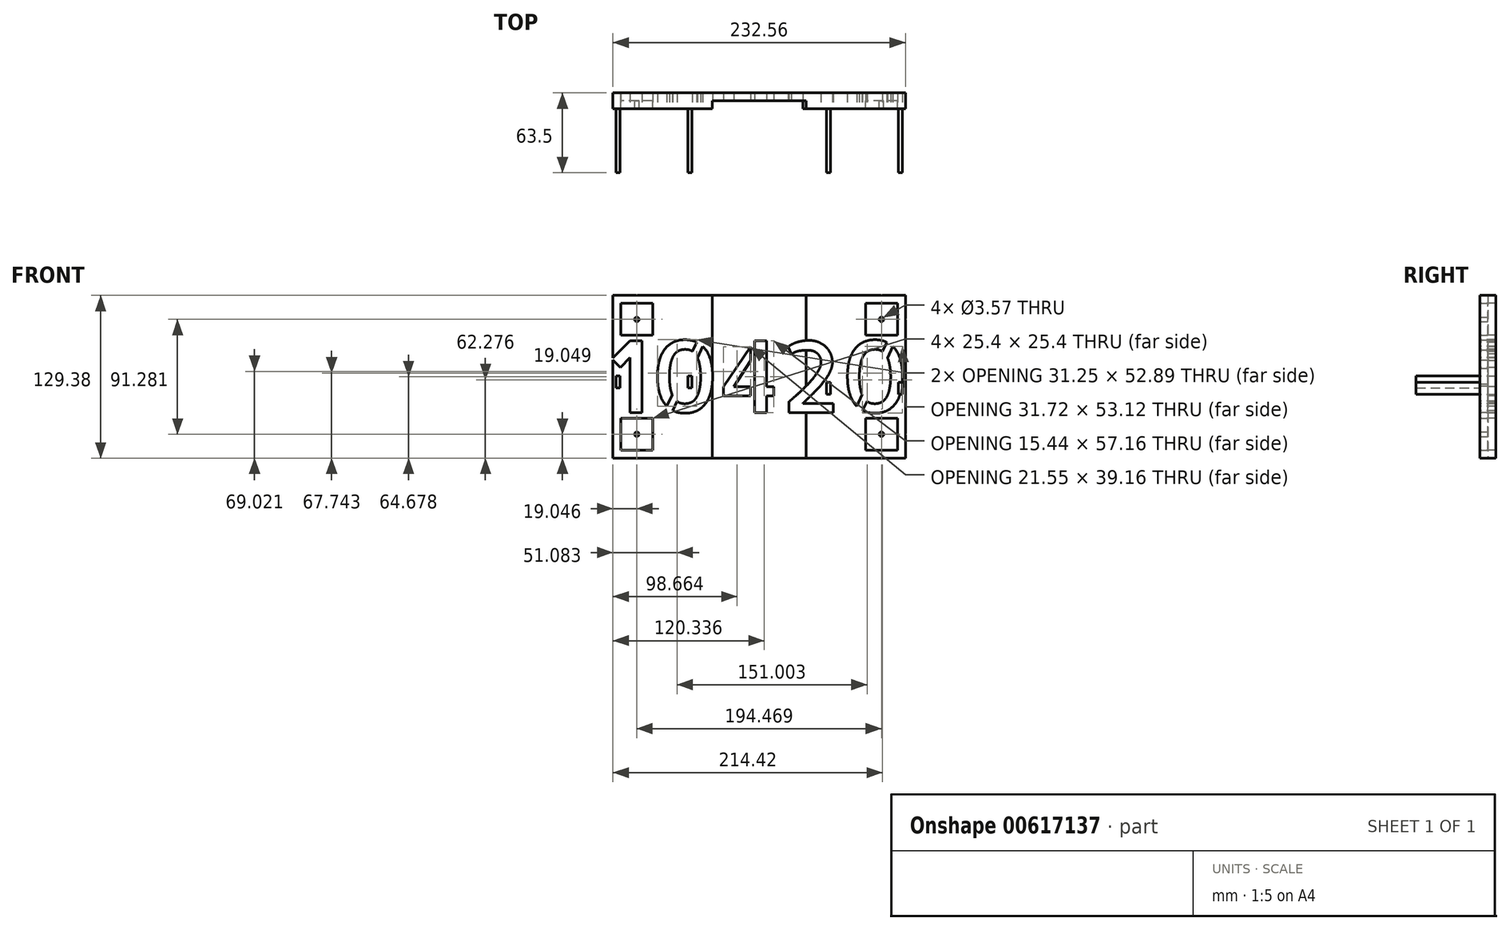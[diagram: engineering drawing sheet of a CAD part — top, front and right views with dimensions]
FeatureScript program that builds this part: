
annotation { "Feature Type Name" : "Feature", "Feature Type Description" : "" }
export const myFeature = defineFeature(function(context is Context, id is Id, definition is map)
    precondition{}
    {
        {
            var Q0;
            Q0=qCreatedBy(makeId("Front.planeOp"),FACE);
            var sketch = newSketch(context, id + "F0", { "sketchPlane" : qUnion([Q0])});
            skLineSegment(sketch, "E0.bottom", {"start": v(-116.28, 64.7) * mm, "end": v(116.28, 64.7) * mm});
            skLineSegment(sketch, "E0.top", {"start": v(-116.28, -64.7) * mm, "end": v(116.28, -64.7) * mm});
            skLineSegment(sketch, "E0.left", {"start": v(-116.28, 64.7) * mm, "end": v(-116.28, -64.7) * mm});
            skPoint(sketch, "E0.middle", {"position": v(0, 0) * mm});
            skLineSegment(sketch, "E1.bottom", {"start": v(-84.53, 32.94) * mm, "end": v(-109.93, 32.94) * mm});
            skLineSegment(sketch, "E1.top", {"start": v(-84.53, 58.34) * mm, "end": v(-109.93, 58.34) * mm});
            skLineSegment(sketch, "E1.left", {"start": v(-84.53, 32.94) * mm, "end": v(-84.53, 58.34) * mm});
            skLineSegment(sketch, "E1.right", {"start": v(-109.93, 32.94) * mm, "end": v(-109.93, 58.34) * mm});
            skLineSegment(sketch, "E2.bottom", {"start": v(-84.53, -58.34) * mm, "end": v(-109.93, -58.34) * mm});
            skLineSegment(sketch, "E2.top", {"start": v(-84.53, -32.94) * mm, "end": v(-109.93, -32.94) * mm});
            skLineSegment(sketch, "E2.left", {"start": v(-84.53, -58.34) * mm, "end": v(-84.53, -32.94) * mm});
            skLineSegment(sketch, "E2.right", {"start": v(-109.93, -58.34) * mm, "end": v(-109.93, -32.94) * mm});
            skPoint(sketch, "E2.middle", {"position": v(-97.23, -45.64) * mm});
            skLineSegment(sketch, "E3.bottom", {"start": v(109.93, 32.94) * mm, "end": v(84.53, 32.94) * mm});
            skLineSegment(sketch, "E3.top", {"start": v(109.93, 58.34) * mm, "end": v(84.53, 58.34) * mm});
            skLineSegment(sketch, "E3.left", {"start": v(109.93, 32.94) * mm, "end": v(109.93, 58.34) * mm});
            skLineSegment(sketch, "E3.right", {"start": v(84.53, 32.94) * mm, "end": v(84.53, 58.34) * mm});
            skPoint(sketch, "E3.middle", {"position": v(97.23, 45.64) * mm});
            skLineSegment(sketch, "E4", {"start": v(116.28, 64.7) * mm, "end": v(116.28, -64.7) * mm});
            skLineSegment(sketch, "E5.bottom", {"start": v(109.93, -58.34) * mm, "end": v(84.53, -58.34) * mm});
            skLineSegment(sketch, "E5.top", {"start": v(109.93, -32.94) * mm, "end": v(84.53, -32.94) * mm});
            skLineSegment(sketch, "E5.left", {"start": v(109.93, -58.34) * mm, "end": v(109.93, -32.94) * mm});
            skLineSegment(sketch, "E5.right", {"start": v(84.53, -58.34) * mm, "end": v(84.53, -32.94) * mm});
            skPoint(sketch, "E5.middle", {"position": v(97.23, -45.64) * mm});
            skPoint(sketch, "E6", {"position": v(-97.23, 45.64) * mm});
            skCircle(sketch, "E7", {"center": v(-97.23, 45.64) * mm, "radius": 1.79 * mm});
            skCircle(sketch, "E8", {"center": v(97.23, 45.64) * mm, "radius": 1.79 * mm});
            skCircle(sketch, "E9", {"center": v(-97.23, -45.64) * mm, "radius": 1.79 * mm});
            skCircle(sketch, "E10", {"center": v(97.23, -45.64) * mm, "radius": 1.79 * mm});
            skSolve(sketch);
        }
        {
            var Q0;
            Q0=makeQuery(id+"F0.imprint","IMPRINT",FACE,{"disambiguationData":[TD([[makeQuery(id+"F0.imprint","IMPRINT",EDGE,{"derivedFrom":sQuery(id+"F0.wireOp",EDGE,"E0.bottom")}),-1.0]])]});
            var Q1;
            Q1=makeQuery(id+"FoGv1v56h3pfjVM_0.opExtrude","SWEPT_BODY",BODY,{"disambiguationData":[OSD([sQuery(id+"F0.wireOp",EDGE,"E5.bottom"),sQuery(id+"F0.wireOp",EDGE,"E5.top"),sQuery(id+"F0.wireOp",EDGE,"E5.left"),sQuery(id+"F0.wireOp",EDGE,"E5.right")])]});
            extrude(context, id + "F1", {"entities" : qUnion([Q0]), "endBound" : BoundingType.SYMMETRIC, "oppositeDirection" : true, "depth" : 12.7 * mm, "endBoundEntityBody" : qUnion([Q1]), "hasOffset" : true, "offsetDistance" : 25.4 * mm});
        }
        {
            var Q0;
            Q0=makeQuery(id+"F1.opExtrude","CAP_FACE",FACE,{"disambiguationData":[OSD([sQuery(id+"F0.wireOp",EDGE,"E0.bottom"),sQuery(id+"F0.wireOp",EDGE,"E0.top"),sQuery(id+"F0.wireOp",EDGE,"E0.left"),sQuery(id+"F0.wireOp",EDGE,"E1.bottom"),sQuery(id+"F0.wireOp",EDGE,"E1.top"),sQuery(id+"F0.wireOp",EDGE,"E1.left"),sQuery(id+"F0.wireOp",EDGE,"E1.right"),sQuery(id+"F0.wireOp",EDGE,"E2.bottom"),sQuery(id+"F0.wireOp",EDGE,"E2.top"),sQuery(id+"F0.wireOp",EDGE,"E2.left"),sQuery(id+"F0.wireOp",EDGE,"E2.right"),sQuery(id+"F0.wireOp",EDGE,"E3.bottom"),sQuery(id+"F0.wireOp",EDGE,"E3.top"),sQuery(id+"F0.wireOp",EDGE,"E3.left"),sQuery(id+"F0.wireOp",EDGE,"E3.right"),sQuery(id+"F0.wireOp",EDGE,"E4"),sQuery(id+"F0.wireOp",EDGE,"E5.bottom"),sQuery(id+"F0.wireOp",EDGE,"E5.top"),sQuery(id+"F0.wireOp",EDGE,"E5.left"),sQuery(id+"F0.wireOp",EDGE,"E5.right")])],"isStart":true});
            var sketch = newSketch(context, id + "F2", { "sketchPlane" : qUnion([Q0])});
            skText(sketch, "E11", { "text": "10420", "fontName": "AllertaStencil-Regular.ttf"});
            const initialGuessF2  = {"E11": [-0.1193, -0.02859, 1, 0, 0.05718]};
            skSetInitialGuess(sketch, initialGuessF2);
            skSolve(sketch);
        }
        {
            var Q0;
            Q0 = qSketchRegion(id + "F2", true);
            var Q1;
            Q1=makeQuery(id+"F2.imprint","IMPRINT",FACE,{"disambiguationData":[TD([[makeQuery(id+"F2.imprint","IMPRINT",EDGE,{"derivedFrom":sQuery(id+"F2.wireOp",EDGE,"4f8eda91-837c-4b1e-aee5-07c52f4a7d4a.sketch_text.stroke-70")}),1.0]])]});
            var Q2;
            Q2=makeQuery(id+"F2.imprint","IMPRINT",FACE,{"disambiguationData":[TD([[makeQuery(id+"F2.imprint","IMPRINT",EDGE,{"derivedFrom":sQuery(id+"F2.wireOp",EDGE,"4f8eda91-837c-4b1e-aee5-07c52f4a7d4a.sketch_text.stroke-17")}),1.0]])]});
            var Q3;
            Q3=makeQuery(id+"F2.imprint","IMPRINT",FACE,{"disambiguationData":[TD([[makeQuery(id+"F2.imprint","IMPRINT",EDGE,{"derivedFrom":sQuery(id+"F2.wireOp",EDGE,"4f8eda91-837c-4b1e-aee5-07c52f4a7d4a.sketch_text.stroke-36")}),1.0]])]});
            extrude(context, id + "F3", {"entities" : qUnion([Q0, Q1, Q2, Q3]), "operationType" : NewBodyOperationType.REMOVE, "oppositeDirection" : true, "depth" : 12.7 * mm, "offsetDistance" : 25.4 * mm});
        }
        {
            var Q0;
            Q0=makeQuery(id+"F0.imprint","IMPRINT",FACE,{"disambiguationData":[TD([[makeQuery(id+"F0.imprint","IMPRINT",EDGE,{"derivedFrom":sQuery(id+"F0.wireOp",EDGE,"E5.bottom")}),-1.0]])]});
            var Q1;
            Q1=makeQuery(id+"F0.imprint","IMPRINT",FACE,{"disambiguationData":[TD([[makeQuery(id+"F0.imprint","IMPRINT",EDGE,{"derivedFrom":sQuery(id+"F0.wireOp",EDGE,"E2.bottom")}),-1.0]])]});
            var Q2;
            Q2=makeQuery(id+"F0.imprint","IMPRINT",FACE,{"disambiguationData":[TD([[makeQuery(id+"F0.imprint","IMPRINT",EDGE,{"derivedFrom":sQuery(id+"F0.wireOp",EDGE,"E3.bottom")}),-1.0]])]});
            var Q3;
            Q3=makeQuery(id+"F0.imprint","IMPRINT",FACE,{"disambiguationData":[TD([[makeQuery(id+"F0.imprint","IMPRINT",EDGE,{"derivedFrom":sQuery(id+"F0.wireOp",EDGE,"E1.bottom")}),-1.0]])]});
            extrude(context, id + "F4", {"entities" : qUnion([Q0, Q1, Q2, Q3]), "depth" : 6.35 * mm, "offsetDistance" : 25.4 * mm});
        }
        {
            var Q0;
            Q0=makeQuery(id+"F1.opExtrude","CAP_FACE",FACE,{"disambiguationData":[OSD([sQuery(id+"F0.wireOp",EDGE,"E0.bottom"),sQuery(id+"F0.wireOp",EDGE,"E0.top"),sQuery(id+"F0.wireOp",EDGE,"E0.left"),sQuery(id+"F0.wireOp",EDGE,"E1.bottom"),sQuery(id+"F0.wireOp",EDGE,"E1.top"),sQuery(id+"F0.wireOp",EDGE,"E1.left"),sQuery(id+"F0.wireOp",EDGE,"E1.right"),sQuery(id+"F0.wireOp",EDGE,"E2.bottom"),sQuery(id+"F0.wireOp",EDGE,"E2.top"),sQuery(id+"F0.wireOp",EDGE,"E2.left"),sQuery(id+"F0.wireOp",EDGE,"E2.right"),sQuery(id+"F0.wireOp",EDGE,"E3.bottom"),sQuery(id+"F0.wireOp",EDGE,"E3.top"),sQuery(id+"F0.wireOp",EDGE,"E3.left"),sQuery(id+"F0.wireOp",EDGE,"E3.right"),sQuery(id+"F0.wireOp",EDGE,"E4"),sQuery(id+"F0.wireOp",EDGE,"E5.bottom"),sQuery(id+"F0.wireOp",EDGE,"E5.top"),sQuery(id+"F0.wireOp",EDGE,"E5.left"),sQuery(id+"F0.wireOp",EDGE,"E5.right")])],"isStart":true});
            var sketch = newSketch(context, id + "F5", { "sketchPlane" : qUnion([Q0])});
            skLineSegment(sketch, "E12.bottom", {"start": v(37.3, 64.7) * mm, "end": v(-37.3, 64.7) * mm});
            skLineSegment(sketch, "E12.top", {"start": v(37.3, -64.7) * mm, "end": v(-37.3, -64.7) * mm});
            skLineSegment(sketch, "E12.left", {"start": v(37.3, 64.7) * mm, "end": v(37.3, -64.7) * mm});
            skLineSegment(sketch, "E12.right", {"start": v(-37.3, 64.7) * mm, "end": v(-37.3, -64.7) * mm});
            skPoint(sketch, "E12.middle", {"position": v(0, 0) * mm});
            skSolve(sketch);
        }
        {
            var Q0;
            {var subQ5=sQuery(id+"F5.wireOp",EDGE,"E12.bottom");Q0=makeQuery(id+"F5.imprint","IMPRINT",FACE,{"disambiguationData":[TD([[makeQuery(id+"F5.imprint","IMPRINT",EDGE,{"derivedFrom":subQ5}),-1.0]])]});}
            extrude(context, id + "F6", {"entities" : qUnion([Q0]), "operationType" : NewBodyOperationType.REMOVE, "oppositeDirection" : true, "depth" : 6.35 * mm, "offsetDistance" : 25.4 * mm});
        }
        {
            var Q0;
            {var subQ3=sQuery(id+"F0.wireOp",EDGE,"E5.right");var subQ4=sQuery(id+"F0.wireOp",EDGE,"E5.left");var subQ5=sQuery(id+"F0.wireOp",EDGE,"E5.top");var subQ6=sQuery(id+"F0.wireOp",EDGE,"E5.bottom");var subQ7=sQuery(id+"F0.wireOp",EDGE,"E4");var subQ8=sQuery(id+"F0.wireOp",EDGE,"E3.right");var subQ9=sQuery(id+"F0.wireOp",EDGE,"E3.left");var subQ11=sQuery(id+"F0.wireOp",EDGE,"E3.top");var subQ12=sQuery(id+"F0.wireOp",EDGE,"E3.bottom");var subQ13=sQuery(id+"F0.wireOp",EDGE,"E2.right");var subQ14=sQuery(id+"F0.wireOp",EDGE,"E0.left");var subQ15=sQuery(id+"F0.wireOp",EDGE,"E0.top");var subQ16=sQuery(id+"F0.wireOp",EDGE,"E1.bottom");var subQ17=sQuery(id+"F0.wireOp",EDGE,"E0.bottom");var subQ18=sQuery(id+"F0.wireOp",EDGE,"E2.left");var subQ19=sQuery(id+"F0.wireOp",EDGE,"E1.top");var subQ20=sQuery(id+"F0.wireOp",EDGE,"E1.left");var subQ21=sQuery(id+"F0.wireOp",EDGE,"E1.right");var subQ22=sQuery(id+"F0.wireOp",EDGE,"E2.bottom");var subQ23=sQuery(id+"F0.wireOp",EDGE,"E2.top");Q0=makeQuery(id+"F6.boolean.opBoolean","SPLIT",FACE,{"disambiguationData":[TD([makeQuery(id+"F1.opExtrude","SWEPT_FACE",FACE,{"disambiguationData":[OSD([subQ17])]})])],"derivedFrom":makeQuery(id+"F1.opExtrude","CAP_FACE",FACE,{"disambiguationData":[OSD([subQ17,subQ15,subQ14,subQ16,subQ19,subQ20,subQ21,subQ22,subQ23,subQ18,subQ13,subQ12,subQ11,subQ9,subQ8,subQ7,subQ6,subQ5,subQ4,subQ3])],"isStart":true})});}
            var sketch = newSketch(context, id + "F7", { "sketchPlane" : qUnion([Q0])});
            skLineSegment(sketch, "E13.bottom", {"start": v(53.42, -4.46) * mm, "end": v(56.6, -4.46) * mm});
            skLineSegment(sketch, "E13.top", {"start": v(53.42, -13.98) * mm, "end": v(56.6, -13.98) * mm});
            skLineSegment(sketch, "E13.left", {"start": v(53.42, -4.46) * mm, "end": v(53.42, -13.98) * mm});
            skLineSegment(sketch, "E13.right", {"start": v(56.6, -4.46) * mm, "end": v(56.6, -13.98) * mm});
            skPoint(sketch, "E13.middle", {"position": v(55, -9.22) * mm});
            skLineSegment(sketch, "E14.bottom", {"start": v(110.57, -13.98) * mm, "end": v(113.74, -13.98) * mm});
            skLineSegment(sketch, "E14.top", {"start": v(110.57, -4.46) * mm, "end": v(113.74, -4.46) * mm});
            skLineSegment(sketch, "E14.left", {"start": v(110.57, -13.98) * mm, "end": v(110.57, -4.46) * mm});
            skLineSegment(sketch, "E14.right", {"start": v(113.74, -13.98) * mm, "end": v(113.74, -4.46) * mm});
            skPoint(sketch, "E14.middle", {"position": v(112.16, -9.22) * mm});
            skLineSegment(sketch, "E15.bottom", {"start": v(-56.6, 0.79) * mm, "end": v(-53.42, 0.79) * mm});
            skLineSegment(sketch, "E15.top", {"start": v(-56.6, -8.74) * mm, "end": v(-53.42, -8.74) * mm});
            skLineSegment(sketch, "E15.left", {"start": v(-56.6, 0.79) * mm, "end": v(-56.6, -8.74) * mm});
            skLineSegment(sketch, "E15.right", {"start": v(-53.42, 0.79) * mm, "end": v(-53.42, -8.74) * mm});
            skPoint(sketch, "E15.middle", {"position": v(-55, -3.97) * mm});
            skLineSegment(sketch, "E16.bottom", {"start": v(-110.57, 0.79) * mm, "end": v(-113.74, 0.79) * mm});
            skLineSegment(sketch, "E16.top", {"start": v(-110.57, -8.74) * mm, "end": v(-113.74, -8.74) * mm});
            skLineSegment(sketch, "E16.left", {"start": v(-110.57, 0.79) * mm, "end": v(-110.57, -8.74) * mm});
            skLineSegment(sketch, "E16.right", {"start": v(-113.74, 0.79) * mm, "end": v(-113.74, -8.74) * mm});
            skPoint(sketch, "E16.middle", {"position": v(-112.16, -3.97) * mm});
            skSolve(sketch);
        }
        {
            var Q0;
            Q0=makeQuery(id+"F7.imprint","IMPRINT",FACE,{"disambiguationData":[TD([[makeQuery(id+"F7.imprint","IMPRINT",EDGE,{"derivedFrom":sQuery(id+"F7.wireOp",EDGE,"E15.bottom")}),-1.0]])]});
            var Q1;
            Q1=makeQuery(id+"F7.imprint","IMPRINT",FACE,{"disambiguationData":[TD([[makeQuery(id+"F7.imprint","IMPRINT",EDGE,{"derivedFrom":sQuery(id+"F7.wireOp",EDGE,"E16.bottom")}),1.0]])]});
            var Q2;
            Q2=makeQuery(id+"F7.imprint","IMPRINT",FACE,{"disambiguationData":[TD([[makeQuery(id+"F7.imprint","IMPRINT",EDGE,{"derivedFrom":sQuery(id+"F7.wireOp",EDGE,"E14.bottom")}),1.0]])]});
            var Q3;
            Q3=makeQuery(id+"F7.imprint","IMPRINT",FACE,{"disambiguationData":[TD([[makeQuery(id+"F7.imprint","IMPRINT",EDGE,{"derivedFrom":sQuery(id+"F7.wireOp",EDGE,"E13.bottom")}),-1.0]])]});
            extrude(context, id + "F8", {"entities" : qUnion([Q0, Q1, Q2, Q3]), "operationType" : NewBodyOperationType.ADD, "depth" : 50.8 * mm, "offsetDistance" : 25.4 * mm});
        }
    });
